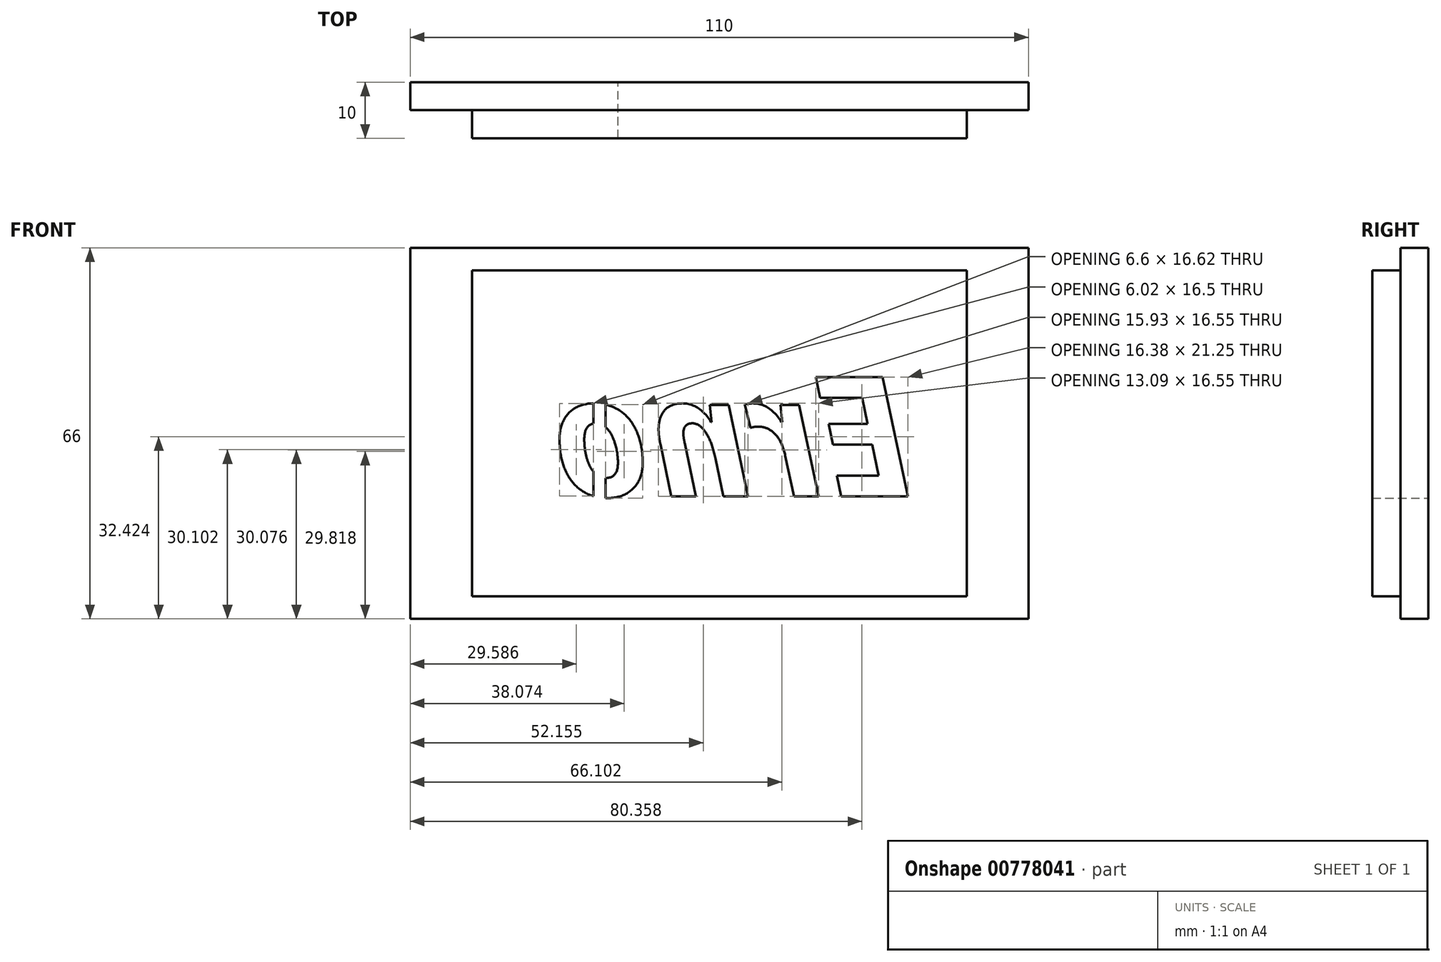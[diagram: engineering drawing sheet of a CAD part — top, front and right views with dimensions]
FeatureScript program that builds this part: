
annotation { "Feature Type Name" : "Feature", "Feature Type Description" : "" }
export const myFeature = defineFeature(function(context is Context, id is Id, definition is map)
    precondition{}
    {
        {
            var Q0;
            Q0=qCreatedBy(makeId("Front.planeOp"),FACE);
            var sketch = newSketch(context, id + "F0", { "sketchPlane" : qUnion([Q0])});
            skLineSegment(sketch, "E0.bottom", {"start": v(55, -33) * mm, "end": v(-55, -33) * mm});
            skLineSegment(sketch, "E0.top", {"start": v(55, 33) * mm, "end": v(-55, 33) * mm});
            skLineSegment(sketch, "E0.left", {"start": v(55, -33) * mm, "end": v(55, 33) * mm});
            skLineSegment(sketch, "E0.right", {"start": v(-55, -33) * mm, "end": v(-55, 33) * mm});
            skPoint(sketch, "E0.middle", {"position": v(0, 0) * mm});
            skSolve(sketch);
        }
        {
            var Q0;
            Q0=makeQuery(id+"F0.imprint","IMPRINT",FACE,{"disambiguationData":[TD([[makeQuery(id+"F0.imprint","IMPRINT",EDGE,{"derivedFrom":sQuery(id+"F0.wireOp",EDGE,"E0.bottom")}),-1.0]])]});
            extrude(context, id + "F1", {"entities" : qUnion([Q0]), "depth" : 5 * mm, "offsetDistance" : 25 * mm});
        }
        {
            var Q0;
            Q0=makeQuery(id+"F1.opExtrude","CAP_FACE",FACE,{"disambiguationData":[OSD([sQuery(id+"F0.wireOp",EDGE,"E0.bottom"),sQuery(id+"F0.wireOp",EDGE,"E0.top"),sQuery(id+"F0.wireOp",EDGE,"E0.left"),sQuery(id+"F0.wireOp",EDGE,"E0.right")])],"isStart":false});
            var sketch = newSketch(context, id + "F2", { "sketchPlane" : qUnion([Q0])});
            skLineSegment(sketch, "E1.bottom", {"start": v(44, -29) * mm, "end": v(-44, -29) * mm});
            skLineSegment(sketch, "E1.top", {"start": v(44, 29) * mm, "end": v(-44, 29) * mm});
            skLineSegment(sketch, "E1.left", {"start": v(44, -29) * mm, "end": v(44, 29) * mm});
            skLineSegment(sketch, "E1.right", {"start": v(-44, -29) * mm, "end": v(-44, 29) * mm});
            skPoint(sketch, "E1.middle", {"position": v(0, 0) * mm});
            skSolve(sketch);
        }
        {
            var Q0;
            Q0=makeQuery(id+"F2.imprint","IMPRINT",FACE,{"disambiguationData":[TD([[makeQuery(id+"F2.imprint","IMPRINT",EDGE,{"derivedFrom":sQuery(id+"F2.wireOp",EDGE,"E1.bottom")}),-1.0]])]});
            extrude(context, id + "F3", {"entities" : qUnion([Q0]), "operationType" : NewBodyOperationType.ADD, "depth" : 5 * mm, "offsetDistance" : 25 * mm});
        }
        {
            var Q0;
            Q0=makeQuery(id+"F1.opExtrude","CAP_FACE",FACE,{"disambiguationData":[OSD([sQuery(id+"F0.wireOp",EDGE,"E0.bottom"),sQuery(id+"F0.wireOp",EDGE,"E0.top"),sQuery(id+"F0.wireOp",EDGE,"E0.left"),sQuery(id+"F0.wireOp",EDGE,"E0.right")])],"isStart":true});
            var sketch = newSketch(context, id + "F4", { "sketchPlane" : qUnion([Q0])});
            skText(sketch, "E2", { "text": "Erno", "fontName": "OpenSans-BoldItalic.ttf"});
            const initialGuessF4  = {"E2": [-0.03432, -0.0112, 1, 0, 0.02143]};
            skSetInitialGuess(sketch, initialGuessF4);
            skSolve(sketch);
        }
        {
            var Q0;
            Q0 = qSketchRegion(id + "F4", true);
            extrude(context, id + "F5", {"entities" : qUnion([Q0]), "operationType" : NewBodyOperationType.REMOVE, "oppositeDirection" : true, "depth" : 25 * mm, "offsetDistance" : 25 * mm});
        }
        {
            var Q0;
            Q0=makeQuery(id+"F5.boolean.opBoolean","SPLIT",FACE,{"disambiguationData":[TD([makeQuery(id+"F5.opExtrude","SWEPT_FACE",FACE,{"disambiguationData":[OSD([sQuery(id+"F4.wireOp",EDGE,"E2.sketch_text.stroke-41")])]})])],"derivedFrom":makeQuery(id+"F3.opExtrude","CAP_FACE",FACE,{"disambiguationData":[OSD([sQuery(id+"F2.wireOp",EDGE,"E1.bottom"),sQuery(id+"F2.wireOp",EDGE,"E1.top"),sQuery(id+"F2.wireOp",EDGE,"E1.left"),sQuery(id+"F2.wireOp",EDGE,"E1.right")])],"isStart":false})});
            var sketch = newSketch(context, id + "F6", { "sketchPlane" : qUnion([Q0])});
            skLineSegment(sketch, "E3.bottom", {"start": v(-20.22, -14.81) * mm, "end": v(-22.4, -14.81) * mm});
            skLineSegment(sketch, "E3.top", {"start": v(-20.22, 5.72) * mm, "end": v(-22.4, 5.72) * mm});
            skLineSegment(sketch, "E3.left", {"start": v(-20.22, -14.81) * mm, "end": v(-20.22, 5.72) * mm});
            skLineSegment(sketch, "E3.right", {"start": v(-22.4, -14.81) * mm, "end": v(-22.4, 5.72) * mm});
            skPoint(sketch, "E3.middle", {"position": v(-21.31, -4.55) * mm});
            skSolve(sketch);
        }
        {
            var Q0;
            {var subQ1=sQuery(id+"F6.wireOp",EDGE,"E3.top");Q0=makeQuery(id+"F6.imprint","IMPRINT",FACE,{"disambiguationData":[TD([[makeQuery(id+"F6.imprint","IMPRINT",EDGE,{"derivedFrom":subQ1}),1.0]])]});}
            var Q1;
            {var subQ2=sQuery(id+"F6.wireOp",EDGE,"E3.bottom");Q1=makeQuery(id+"F6.imprint","IMPRINT",FACE,{"disambiguationData":[TD([[makeQuery(id+"F6.imprint","IMPRINT",EDGE,{"derivedFrom":subQ2}),-1.0]])]});}
            extrude(context, id + "F7", {"entities" : qUnion([Q0, Q1]), "operationType" : NewBodyOperationType.ADD, "oppositeDirection" : true, "depth" : 10 * mm, "offsetDistance" : 25 * mm});
        }
    });
